# Revit family: Neptun Maxima Parallel
name_source: partatom
category: HLS-Bauteile
units: mm (PartAtom-declared; Revit-internal decimal feet)

## family parameters
Arbeitsebenenbasiert = Nein
Beim Laden mit Abzugskörper schneiden = Nein
Bemaßung runder Anschluss = Durchmesser verwenden
Beschriftungsausrichtung beibehalten = Nein
Gemeinsam genutzt = Nein
Immer vertikal = Ja
Klassifizierung = Keine
Raumberechnungspunkt = Nein
Teiletyp = Normal

## types (5) — shared parameters
Anschluss_1" = 25 mm  [stored 0.082021 ft]
Anschluss_2" = 50 mm  [stored 0.164042 ft]
Datenblatt = https://www.burkhalter-h2o.ch
Homepage = https://www.burkhalter-h2o.ch
LUT = LUT_Neptun_Maxima
Sockel_Höhe = 150 mm  [stored 0.492126 ft]
Steuerung_Breite = 200 mm  [stored 0.656168 ft]
Steuerung_Höhe = 250 mm  [stored 0.82021 ft]
Steuerung_Tiefe = 75 mm  [stored 0.246063 ft]
zero-valued in all types: Vorgabe-Ansicht

## per-type parameters (varying)
| type | A | B | Behälterkopf | C | Harzinhalt_pro_Harzdruckbehälter | Sockel_Absatz_Oben | Sockel_Absatz_Unten | X |
| Neptun Maxima - 150L | 552 mm  [stored 1.81102 ft] | 1900 mm  [stored 6.2336 ft] | 250 mm  [stored 0.82021 ft] | 1730 mm  [stored 5.67585 ft] | 150L | 226 mm  [stored 0.74147 ft] | 286 mm  [stored 0.93832 ft] | 750 mm  [stored 2.46063 ft] |
| Neptun Maxima - 200L | 552 mm  [stored 1.81102 ft] | 1900 mm  [stored 6.2336 ft] | 250 mm  [stored 0.82021 ft] | 1730 mm  [stored 5.67585 ft] | 200L | 226 mm  [stored 0.74147 ft] | 286 mm  [stored 0.93832 ft] | 750 mm  [stored 2.46063 ft] |
| Neptun Maxima - 250L | 610 mm  [stored 2.00131 ft] | 2120 mm  [stored 6.95538 ft] | 250 mm  [stored 0.82021 ft] | 1950 mm  [stored 6.39764 ft] | 250L | 255 mm | 315 mm  [stored 1.03346 ft] | 850 mm  [stored 2.78871 ft] |
| Neptun Maxima - 300L | 610 mm  [stored 2.00131 ft] | 2120 mm  [stored 6.95538 ft] | 250 mm  [stored 0.82021 ft] | 1950 mm  [stored 6.39764 ft] | 300L | 255 mm | 315 mm  [stored 1.03346 ft] | 850 mm  [stored 2.78871 ft] |
| Neptun Maxima - 400L | 770 mm  [stored 2.52625 ft] | 2315 mm  [stored 7.59514 ft] | 350 mm  [stored 1.14829 ft] | 2110 mm  [stored 6.92257 ft] | 400L | 335 mm  [stored 1.09908 ft] | 395 mm  [stored 1.29593 ft] | 1000 mm  [stored 3.28084 ft] |

note: [stored X ft] marks values corroborated as IEEE doubles in the binary element streams (Revit-internal decimal feet)
